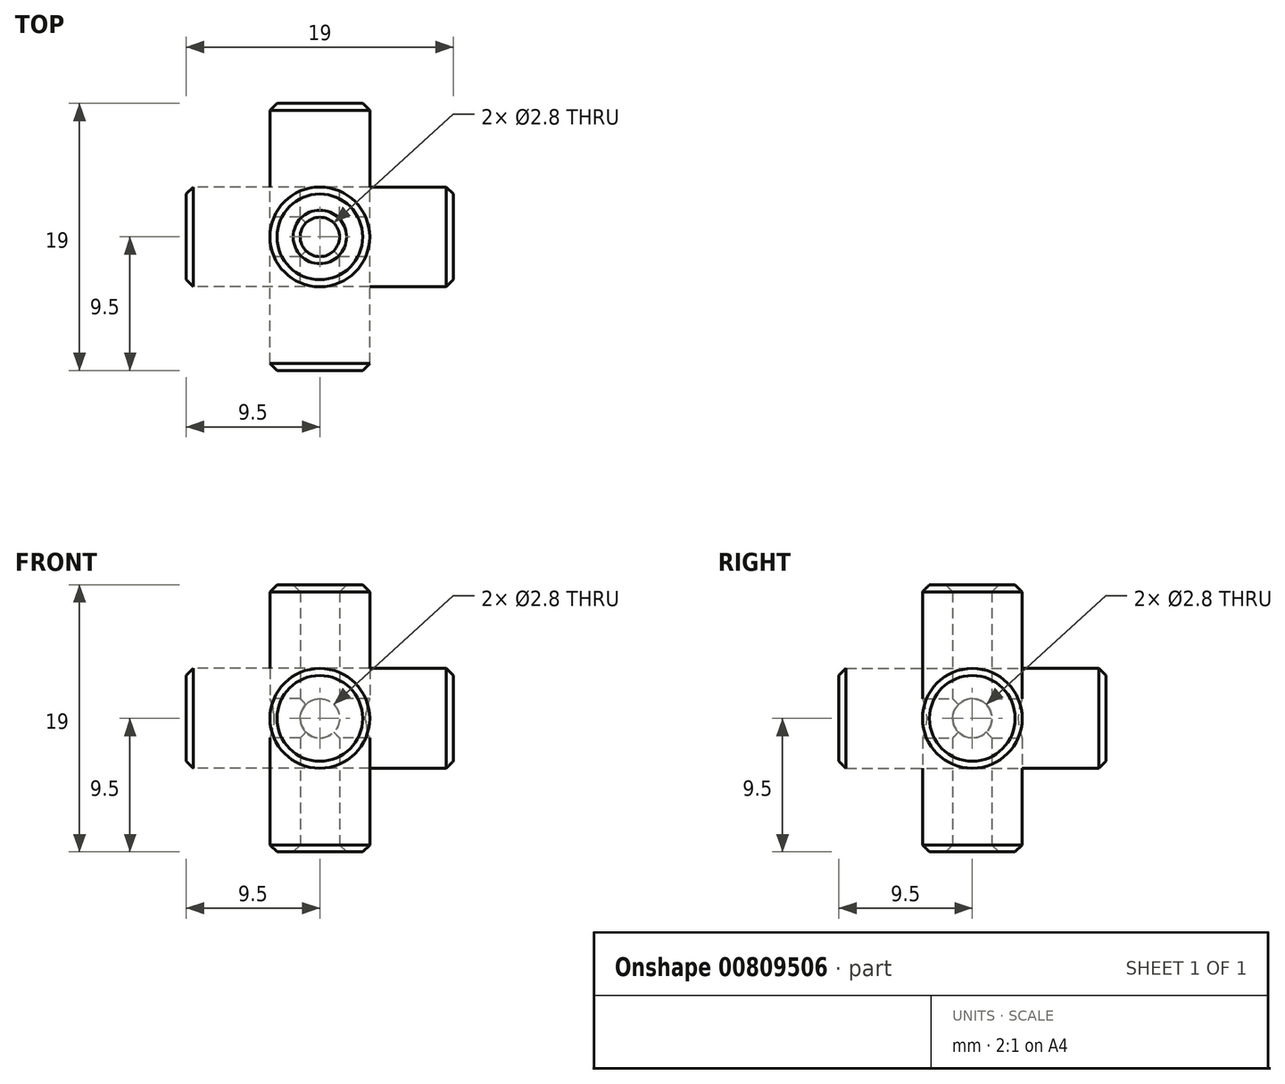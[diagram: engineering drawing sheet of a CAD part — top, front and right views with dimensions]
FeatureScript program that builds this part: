
annotation { "Feature Type Name" : "Feature", "Feature Type Description" : "" }
export const myFeature = defineFeature(function(context is Context, id is Id, definition is map)
    precondition{}
    {
        {
            var Q0;
            Q0=qCreatedBy(makeId("Front.planeOp"),FACE);
            var sketch = newSketch(context, id + "F0", { "sketchPlane" : qUnion([Q0])});
            skCircle(sketch, "E0", {"center": v(0, 0) * mm, "radius": 3.55 * mm});
            skSolve(sketch);
        }
        {
            var Q0;
            Q0 = qSketchRegion(id + "F0", true);
            extrude(context, id + "F1", {"entities" : qUnion([Q0]), "endBound" : BoundingType.SYMMETRIC, "depth" : 19 * mm, "offsetDistance" : 25.4 * mm});
        }
        {
            var Q0;
            Q0=qCreatedBy(makeId("Front.planeOp"),FACE);
            var sketch = newSketch(context, id + "F2", { "sketchPlane" : qUnion([Q0])});
            skCircle(sketch, "E1", {"center": v(0, 0) * mm, "radius": 1.4 * mm});
            skSolve(sketch);
        }
        {
            var Q0;
            Q0 = qSketchRegion(id + "F2", true);
            extrude(context, id + "F3", {"entities" : qUnion([Q0]), "endBound" : BoundingType.SYMMETRIC, "depth" : 20 * mm, "offsetDistance" : 25.4 * mm});
        }
        {
            var Q0;
            Q0=qCreatedBy(makeId("Front.planeOp"),FACE);
            var sketch = newSketch(context, id + "F4", { "sketchPlane" : qUnion([Q0])});
            skLineSegment(sketch, "E2.bottom", {"start": v(0, 0) * mm, "end": v(10, 0) * mm});
            skLineSegment(sketch, "E2.top", {"start": v(0, 10) * mm, "end": v(10, 10) * mm});
            skLineSegment(sketch, "E2.left", {"start": v(0, 0) * mm, "end": v(0, 10) * mm});
            skLineSegment(sketch, "E2.right", {"start": v(10, 0) * mm, "end": v(10, 10) * mm});
            skSolve(sketch);
        }
        {
            var Q0;
            Q0 = qSketchRegion(id + "F4", true);
            extrude(context, id + "F5", {"entities" : qUnion([Q0]), "depth" : 10 * mm, "offsetDistance" : 25 * mm});
        }
        {
            var Q0;
            Q0=qCreatedBy(makeId("Origin.pointOp"),VERTEX);
            var Q1;
            Q1=makeQuery(id+"F5.opExtrude","CAP_VERTEX",VERTEX,{"disambiguationData":[OSD([sQuery(id+"F4.wireOp",EDGE,"E2.top"),sQuery(id+"F4.wireOp",EDGE,"E2.right")])],"isStart":false});
            var Q2;
            Q2=makeQuery(id+"F5.opExtrude","CAP_VERTEX",VERTEX,{"disambiguationData":[OSD([sQuery(id+"F4.wireOp",EDGE,"E2.bottom"),sQuery(id+"F4.wireOp",EDGE,"E2.right")])],"isStart":false});
            cPlane(context, id + "F6", {"entities" : qUnion([Q0, Q1, Q2]), "cplaneType" : CPlaneType.THREE_POINT, "offset" : 25 * mm, "width" : 150 * mm, "height" : 150 * mm});
        }
        {
            var Q0;
            Q0=qCreatedBy(id+"F6.planeOp",FACE);
            var sketch = newSketch(context, id + "F7", { "sketchPlane" : qUnion([Q0])});
            skLineSegment(sketch, "E3", {"start": v(0, 0) * mm, "end": v(14.14, 10) * mm});
            skSolve(sketch);
        }
        {
            var Q0;
            Q0=makeQuery(id+"F5.opExtrude","SWEPT_BODY",BODY,{"disambiguationData":[OSD([sQuery(id+"F4.wireOp",EDGE,"E2.bottom"),sQuery(id+"F4.wireOp",EDGE,"E2.top"),sQuery(id+"F4.wireOp",EDGE,"E2.left"),sQuery(id+"F4.wireOp",EDGE,"E2.right")])]});
            deleteBodies(context, id + "F8", {"entities" : qUnion([Q0])});
        }
        {
            var Q0;
            Q0=makeQuery(id+"F3.opExtrude","SWEPT_BODY",BODY,{"disambiguationData":[OSD([sQuery(id+"F2.wireOp",EDGE,"E1")])]});
            var Q1;
            Q1=makeQuery(id+"F1.opExtrude","SWEPT_BODY",BODY,{"disambiguationData":[OSD([sQuery(id+"F0.wireOp",EDGE,"E0")])]});
            var Q2;
            Q2=sQuery(id+"F7.wireOp",EDGE,"E3");
            circularPattern(context, id + "F9", {"entities" : qUnion([Q0, Q1]), "axis" : qUnion([Q2]), "angle" : 360 * degree, "instanceCount" : 3, "equalSpace" : true});
        }
        {
            var Q0;
            Q0=makeQuery(id+"F9.opPattern","COPY",BODY,{"derivedFrom":makeQuery(id+"F3.opExtrude","SWEPT_BODY",BODY,{"disambiguationData":[OSD([sQuery(id+"F2.wireOp",EDGE,"E1")])]}),"instanceName":"2"});
            var Q1;
            Q1=makeQuery(id+"F9.opPattern","COPY",BODY,{"derivedFrom":makeQuery(id+"F3.opExtrude","SWEPT_BODY",BODY,{"disambiguationData":[OSD([sQuery(id+"F2.wireOp",EDGE,"E1")])]}),"instanceName":"1"});
            var Q2;
            Q2=makeQuery(id+"F3.opExtrude","SWEPT_BODY",BODY,{"disambiguationData":[OSD([sQuery(id+"F2.wireOp",EDGE,"E1")])]});
            var Q3;
            Q3=makeQuery(id+"F9.opPattern","COPY",BODY,{"derivedFrom":makeQuery(id+"F1.opExtrude","SWEPT_BODY",BODY,{"disambiguationData":[OSD([sQuery(id+"F0.wireOp",EDGE,"E0")])]}),"instanceName":"2"});
            booleanBodies(context, id + "F10", {"operationType" : BooleanOperationType.SUBTRACTION, "tools" : qUnion([Q0, Q1, Q2]), "targets" : qUnion([Q3])});
        }
        {
            var Q0;
            Q0=makeQuery(id+"F1.opExtrude","CAP_FACE",FACE,{"disambiguationData":[OSD([sQuery(id+"F0.wireOp",EDGE,"E0")])],"isStart":false});
            var Q1;
            Q1=makeQuery(id+"F9.opPattern","COPY",FACE,{"derivedFrom":makeQuery(id+"F1.opExtrude","CAP_FACE",FACE,{"disambiguationData":[OSD([sQuery(id+"F0.wireOp",EDGE,"E0")])],"isStart":true}),"instanceName":"1"});
            var Q2;
            Q2=makeQuery(id+"F9.opPattern","COPY",FACE,{"derivedFrom":makeQuery(id+"F1.opExtrude","CAP_FACE",FACE,{"disambiguationData":[OSD([sQuery(id+"F0.wireOp",EDGE,"E0")])],"isStart":false}),"instanceName":"2"});
            var Q3;
            Q3=makeQuery(id+"F9.opPattern","COPY",FACE,{"derivedFrom":makeQuery(id+"F1.opExtrude","CAP_FACE",FACE,{"disambiguationData":[OSD([sQuery(id+"F0.wireOp",EDGE,"E0")])],"isStart":false}),"instanceName":"1"});
            var Q4;
            Q4=makeQuery(id+"F1.opExtrude","CAP_FACE",FACE,{"disambiguationData":[OSD([sQuery(id+"F0.wireOp",EDGE,"E0")])],"isStart":true});
            var Q5;
            Q5=makeQuery(id+"F9.opPattern","COPY",FACE,{"derivedFrom":makeQuery(id+"F1.opExtrude","CAP_FACE",FACE,{"disambiguationData":[OSD([sQuery(id+"F0.wireOp",EDGE,"E0")])],"isStart":true}),"instanceName":"2"});
            chamfer(context, id + "F11", {"entities" : qUnion([Q0, Q1, Q2, Q3, Q4, Q5]), "width" : 0.5 * mm, "tangentPropagation" : true});
        }
    });
